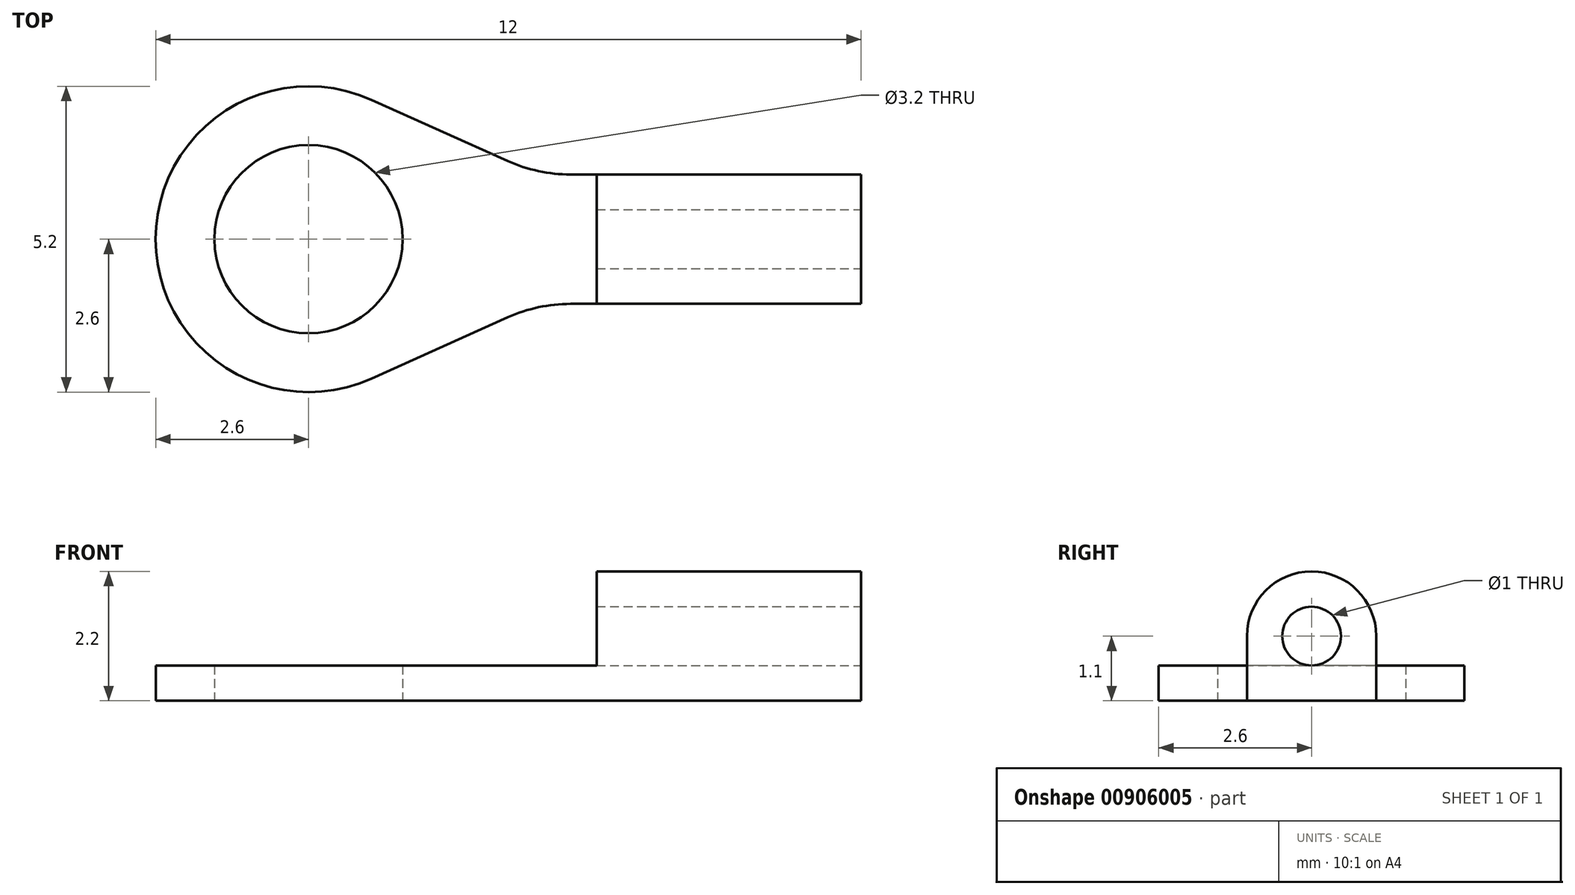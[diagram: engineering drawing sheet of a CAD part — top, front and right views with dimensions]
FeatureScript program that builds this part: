
annotation { "Feature Type Name" : "Feature", "Feature Type Description" : "" }
export const myFeature = defineFeature(function(context is Context, id is Id, definition is map)
    precondition{}
    {
        {
            var Q0;
            Q0=qCreatedBy(makeId("Top.planeOp"),FACE);
            var sketch = newSketch(context, id + "F0", { "sketchPlane" : qUnion([Q0])});
            skLineSegment(sketch, "E0", {"start": v(2.6, 0) * mm, "end": v(3.16, 0) * mm});
            skLineSegment(sketch, "E1", {"start": v(12, 1.5) * mm, "end": v(12, 3.7) * mm});
            skLineSegment(sketch, "E2", {"start": v(0, 2.6) * mm, "end": v(0, 2.6) * mm});
            skPoint(sketch, "E3.visualSharp", {"position": v(0, 5.2) * mm});
            skArc(sketch, "E3.filletArc", {"start": v(2.6, 5.2) * mm, "mid": v(0.76, 4.44) * mm, "end": v(0, 2.6) * mm});
            skPoint(sketch, "E4.visualSharp", {"position": v(0, 0) * mm});
            skArc(sketch, "E4.filletArc", {"start": v(0, 2.6) * mm, "mid": v(0.76, 0.76) * mm, "end": v(2.6, 0) * mm});
            skLineSegment(sketch, "E5.0", {"start": v(7.5, 1.5) * mm, "end": v(7.5, 3.7) * mm});
            skLineSegment(sketch, "E6.0", {"start": v(6.5, 1.44) * mm, "end": v(6.5, 1.5) * mm});
            skLineSegment(sketch, "E7.0", {"start": v(2.6, 0) * mm, "end": v(2.6, 5.2) * mm});
            skCircle(sketch, "E8", {"center": v(2.6, 2.6) * mm, "radius": 1.6 * mm});
            skLineSegment(sketch, "E9.0", {"start": v(12, 3.7) * mm, "end": v(7.06, 3.7) * mm});
            skLineSegment(sketch, "E10.0", {"start": v(12, 1.5) * mm, "end": v(7.06, 1.5) * mm});
            skCircle(sketch, "E11", {"center": v(2.6, 2.6) * mm, "radius": 2.6 * mm});
            skLineSegment(sketch, "E12", {"start": v(6, 3.93) * mm, "end": v(3.66, 4.97) * mm});
            skLineSegment(sketch, "E13", {"start": v(6, 1.27) * mm, "end": v(3.66, 0.23) * mm});
            skPoint(sketch, "E14.visualSharp", {"position": v(6.5, 3.7) * mm});
            skArc(sketch, "E14.filletArc", {"start": v(6, 3.93) * mm, "mid": v(6.51, 3.76) * mm, "end": v(7.06, 3.7) * mm});
            skPoint(sketch, "E15.visualSharp", {"position": v(6.5, 1.5) * mm});
            skArc(sketch, "E15.filletArc", {"start": v(7.06, 1.5) * mm, "mid": v(6.51, 1.44) * mm, "end": v(6, 1.27) * mm});
            skPoint(sketch, "E16.orphan", {"position": v(3.16, 0) * mm});
            skLineSegment(sketch, "E17.trimOffspring", {"start": v(6.5, 3.7) * mm, "end": v(6.5, 3.76) * mm});
            skPoint(sketch, "E18.orphan", {"position": v(7.5, 5.2) * mm});
            skPoint(sketch, "E19.orphan", {"position": v(12, 5.2) * mm});
            skPoint(sketch, "E20.orphan", {"position": v(12, 0) * mm});
            skPoint(sketch, "E21.orphan", {"position": v(7.5, 0) * mm});
            skPoint(sketch, "E22.end.orphan", {"position": v(7.5, 2.6) * mm});
            skPoint(sketch, "E22.start.orphan", {"position": v(12, 2.6) * mm});
            skSolve(sketch);
        }
        {
            var Q0;
            {var subQ0=sQuery(id+"F0.wireOp",EDGE,"E1");Q0=makeQuery(id+"F0.imprint","IMPRINT",FACE,{"disambiguationData":[TD([[makeQuery(id+"F0.imprint","IMPRINT",EDGE,{"derivedFrom":subQ0}),1.0]])]});}
            var Q1;
            Q1 = qSketchRegion(id + "F0", true);
            extrude(context, id + "F1", {"entities" : qUnion([Q0, Q1]), "depth" : 0.6 * mm, "offsetDistance" : 25 * mm});
        }
        {
            var Q0;
            Q0=makeQuery(id+"F1.opExtrude","CAP_FACE",FACE,{"disambiguationData":[OSD([sQuery(id+"F0.wireOp",EDGE,"E1"),sQuery(id+"F0.wireOp",EDGE,"E8"),sQuery(id+"F0.wireOp",EDGE,"E9.0"),sQuery(id+"F0.wireOp",EDGE,"E10.0"),sQuery(id+"F0.wireOp",EDGE,"E11"),sQuery(id+"F0.wireOp",EDGE,"E12"),sQuery(id+"F0.wireOp",EDGE,"E13"),sQuery(id+"F0.wireOp",EDGE,"E14.filletArc"),sQuery(id+"F0.wireOp",EDGE,"E15.filletArc")])],"isStart":false});
            var sketch = newSketch(context, id + "F2", { "sketchPlane" : qUnion([Q0])});
            skLineSegment(sketch, "E23.bottom", {"start": v(12, 3.7) * mm, "end": v(7.5, 3.7) * mm});
            skLineSegment(sketch, "E23.top", {"start": v(12, 1.5) * mm, "end": v(7.5, 1.5) * mm});
            skLineSegment(sketch, "E23.left", {"start": v(12, 3.7) * mm, "end": v(12, 1.5) * mm});
            skLineSegment(sketch, "E23.right", {"start": v(7.5, 3.7) * mm, "end": v(7.5, 1.5) * mm});
            skSolve(sketch);
        }
        {
            var Q0;
            Q0 = qSketchRegion(id + "F2", true);
            extrude(context, id + "F3", {"entities" : qUnion([Q0]), "operationType" : NewBodyOperationType.ADD, "depth" : 1.6 * mm, "offsetDistance" : 25 * mm});
        }
        {
            var Q0;
            Q0=makeQuery(id+"F3.opExtrude","CAP_EDGE",EDGE,{"disambiguationData":[OSD([sQuery(id+"F2.wireOp",EDGE,"E23.bottom")])],"isStart":false});
            var Q1;
            Q1=makeQuery(id+"F3.opExtrude","CAP_EDGE",EDGE,{"disambiguationData":[OSD([sQuery(id+"F2.wireOp",EDGE,"E23.top")])],"isStart":false});
            fillet(context, id + "F4", {"entities" : qUnion([Q0, Q1]), "radius" : 1.1 * mm, "tangentPropagation" : true, "allowEdgeOverflow" : false});
        }
        {
            var Q0;
            Q0=makeQuery(id+"F3.boolean.opBoolean","MERGE",FACE,{"derivedFrom":[makeQuery(id+"F1.opExtrude","SWEPT_FACE",FACE,{"disambiguationData":[OSD([sQuery(id+"F0.wireOp",EDGE,"E1")])]}),makeQuery(id+"F3.opExtrude","SWEPT_FACE",FACE,{"disambiguationData":[OSD([sQuery(id+"F2.wireOp",EDGE,"E23.left")])]})]});
            var sketch = newSketch(context, id + "F5", { "sketchPlane" : qUnion([Q0])});
            skCircle(sketch, "E24", {"center": v(2.6, 1.1) * mm, "radius": 0.5 * mm});
            skSolve(sketch);
        }
        {
            var Q0;
            Q0 = qSketchRegion(id + "F5", true);
            extrude(context, id + "F6", {"entities" : qUnion([Q0]), "operationType" : NewBodyOperationType.REMOVE, "oppositeDirection" : true, "depth" : 25 * mm, "offsetDistance" : 25 * mm});
        }
    });
